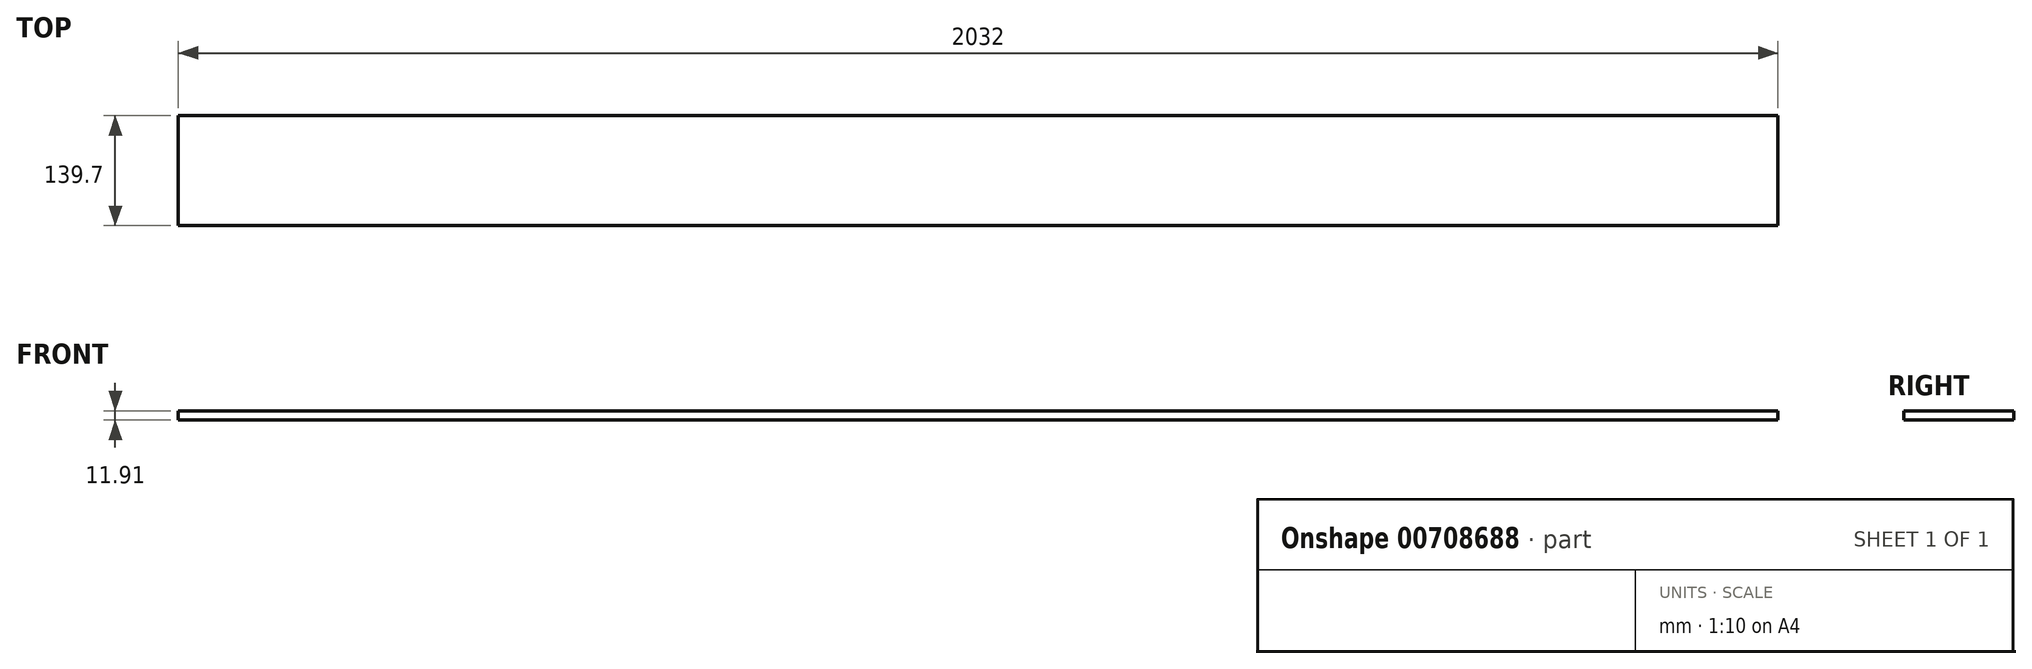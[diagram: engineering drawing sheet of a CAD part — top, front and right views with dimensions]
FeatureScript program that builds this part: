
annotation { "Feature Type Name" : "Feature", "Feature Type Description" : "" }
export const myFeature = defineFeature(function(context is Context, id is Id, definition is map)
    precondition{}
    {
        {
            var Q0;
            Q0=qCreatedBy(makeId("Top.planeOp"),FACE);
            var sketch = newSketch(context, id + "F0", { "sketchPlane" : qUnion([Q0])});
            skLineSegment(sketch, "E0.bottom", {"start": v(1016, -69.85) * mm, "end": v(-1016, -69.85) * mm});
            skLineSegment(sketch, "E0.top", {"start": v(1016, 69.85) * mm, "end": v(-1016, 69.85) * mm});
            skLineSegment(sketch, "E0.left", {"start": v(1016, -69.85) * mm, "end": v(1016, 69.85) * mm});
            skLineSegment(sketch, "E0.right", {"start": v(-1016, -69.85) * mm, "end": v(-1016, 69.85) * mm});
            skPoint(sketch, "E0.middle", {"position": v(0, 0) * mm});
            skSolve(sketch);
        }
        {
            var Q0;
            Q0=makeQuery(id+"F0.imprint","IMPRINT",FACE,{"disambiguationData":[TD([[makeQuery(id+"F0.imprint","IMPRINT",EDGE,{"derivedFrom":sQuery(id+"F0.wireOp",EDGE,"E0.bottom")}),-1.0]])]});
            extrude(context, id + "F1", {"entities" : qUnion([Q0]), "depth" : 11.9 * mm, "offsetDistance" : 25.4 * mm});
        }
    });
